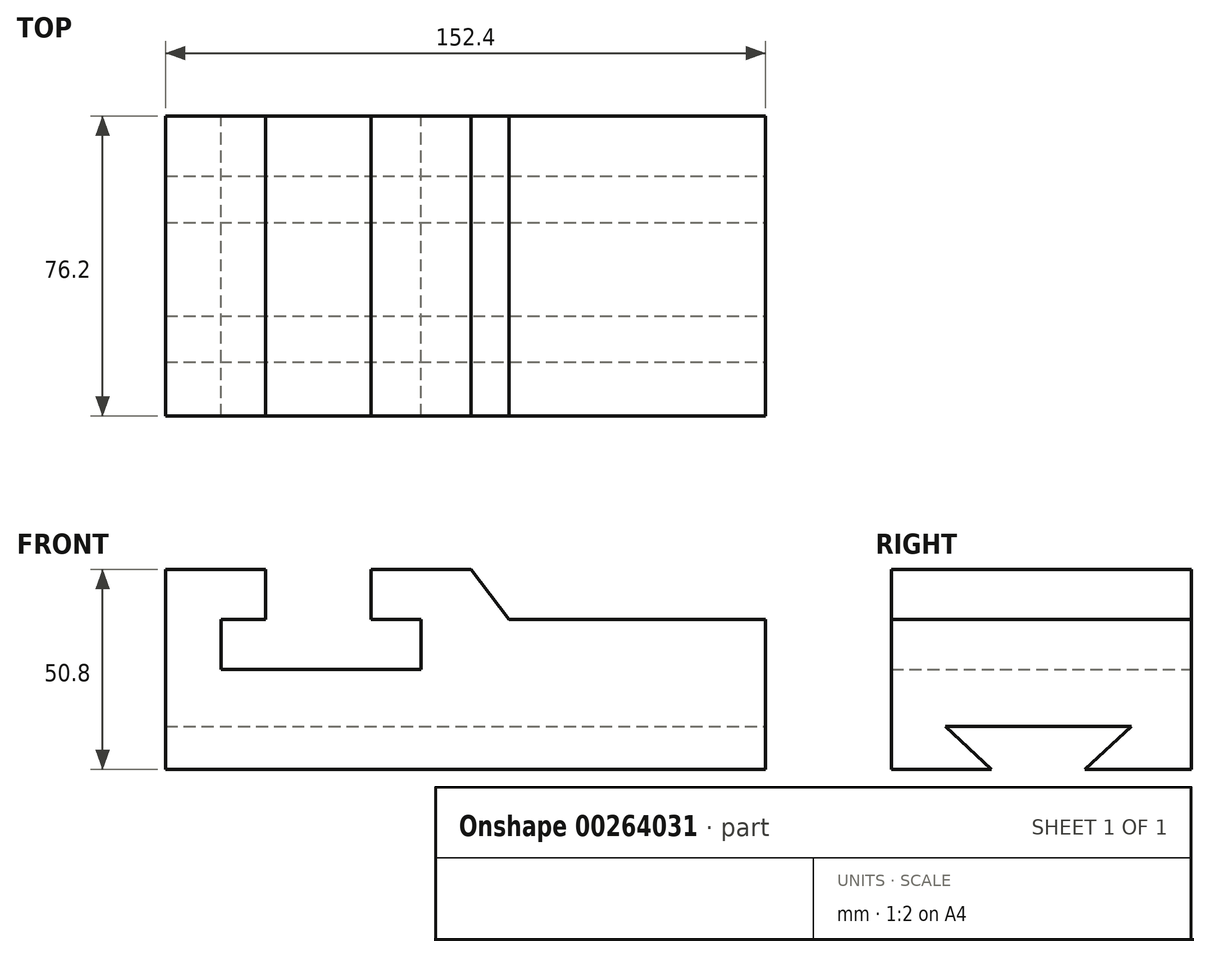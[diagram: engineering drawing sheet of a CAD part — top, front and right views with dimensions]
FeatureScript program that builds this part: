
annotation { "Feature Type Name" : "Feature", "Feature Type Description" : "" }
export const myFeature = defineFeature(function(context is Context, id is Id, definition is map)
    precondition{}
    {
        {
            var Q0;
            Q0=qCreatedBy(makeId("Front.planeOp"),FACE);
            var sketch = newSketch(context, id + "F0", { "sketchPlane" : qUnion([Q0])});
            skLineSegment(sketch, "E0", {"start": v(-76.56, 0) * mm, "end": v(75.84, 0) * mm});
            skLineSegment(sketch, "E1", {"start": v(-76.56, 0) * mm, "end": v(-76.56, 50.8) * mm});
            skLineSegment(sketch, "E2", {"start": v(-76.56, 50.8) * mm, "end": v(-51.16, 50.8) * mm});
            skLineSegment(sketch, "E3", {"start": v(-51.16, 50.8) * mm, "end": v(-51.16, 38.1) * mm});
            skLineSegment(sketch, "E4", {"start": v(-51.16, 38.1) * mm, "end": v(-62.45, 38.1) * mm});
            skLineSegment(sketch, "E5", {"start": v(-62.45, 38.1) * mm, "end": v(-62.45, 25.4) * mm});
            skLineSegment(sketch, "E6", {"start": v(-62.45, 25.4) * mm, "end": v(-11.65, 25.4) * mm});
            skLineSegment(sketch, "E7", {"start": v(-11.65, 25.4) * mm, "end": v(-11.65, 38.1) * mm});
            skLineSegment(sketch, "E8", {"start": v(-11.65, 38.1) * mm, "end": v(-24.35, 38.1) * mm});
            skLineSegment(sketch, "E9", {"start": v(-24.35, 38.1) * mm, "end": v(-24.35, 50.8) * mm});
            skLineSegment(sketch, "E10", {"start": v(-24.35, 50.8) * mm, "end": v(1.05, 50.8) * mm});
            skLineSegment(sketch, "E11", {"start": v(75.84, 0) * mm, "end": v(75.84, 38.1) * mm});
            skLineSegment(sketch, "E12", {"start": v(75.84, 38.1) * mm, "end": v(39.72, 38.1) * mm});
            skLineSegment(sketch, "E13", {"start": v(39.72, 38.1) * mm, "end": v(10.65, 38.1) * mm});
            skLineSegment(sketch, "E14", {"start": v(10.65, 38.1) * mm, "end": v(1.05, 50.8) * mm});
            skSolve(sketch);
        }
        {
            var Q0;
            Q0=makeQuery(id+"F0.imprint","IMPRINT",FACE,{"disambiguationData":[TD([[makeQuery(id+"F0.imprint","IMPRINT",EDGE,{"derivedFrom":sQuery(id+"F0.wireOp",EDGE,"E0")}),1.0]])]});
            extrude(context, id + "F1", {"entities" : qUnion([Q0]), "depth" : 76.2 * mm});
        }
        {
            var Q0;
            Q0=makeQuery(id+"F1.opExtrude","SWEPT_FACE",FACE,{"disambiguationData":[OSD([sQuery(id+"F0.wireOp",EDGE,"E11")])]});
            var sketch = newSketch(context, id + "F2", { "sketchPlane" : qUnion([Q0])});
            skLineSegment(sketch, "E15", {"start": v(-50.8, 0) * mm, "end": v(-62.45, 10.94) * mm});
            skLineSegment(sketch, "E16", {"start": v(-62.45, 10.94) * mm, "end": v(-15.25, 10.94) * mm});
            skLineSegment(sketch, "E17", {"start": v(-15.25, 10.94) * mm, "end": v(-27.05, 0) * mm});
            skLineSegment(sketch, "E18", {"start": v(-27.05, 0) * mm, "end": v(-50.8, 0) * mm});
            skSolve(sketch);
        }
        {
            var Q0;
            Q0=makeQuery(id+"F2.imprint","IMPRINT",FACE,{"disambiguationData":[TD([[makeQuery(id+"F2.imprint","IMPRINT",EDGE,{"derivedFrom":sQuery(id+"F2.wireOp",EDGE,"E15")}),-1.0]])]});
            extrude(context, id + "F3", {"entities" : qUnion([Q0]), "operationType" : NewBodyOperationType.REMOVE, "endBound" : BoundingType.UP_TO_NEXT, "oppositeDirection" : true, "depth" : 25.4 * mm});
        }
    });
